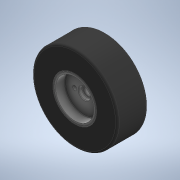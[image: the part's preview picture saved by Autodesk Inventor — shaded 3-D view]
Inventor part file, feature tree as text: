
AUTODESK INVENTOR PART (.ipt)
format: ipt  version: 2022 (Build 260153000, 153)  size: 370,688 bytes
history: native  units: in
note: dims shown in document units (in); Inventor stores cm internally (conversion verified against a paired STEP export)
features: fillet x3, sketch x3, extrude x2, revolve x1
ambient origin geometry x8: Origin, YZ Plane, XZ Plane, XY Plane, X Axis, Y Axis, Z Axis, Center Point
bodies: Solid1 (feature_tree)
feature tree (9):
  revolve  "Revolution1"  [1 undecoded]
  fillet  "Fillet1"  Radius=0.6875in
  fillet  "Fillet2"  Radius=0.0625in
  extrude  "Extrusion1"  Depth=0.125in
  extrude  "Extrusion2"  Depth=0.1875in
  fillet  "Fillet3"  Radius=0.3125in
  sketch  "Sketch1"  dims[d0=1.4in d1=1.0in d2=0.6875in d3=0.0625in]
  sketch  "Sketch2"  dims[d4=0.3125in d5=0.5625in d6=0.125in]
  sketch  "Sketch3"  dims[d7=0.275in d9=0.1875in d10=0.3125in d11=0.125in d12=360.0deg d13=0.0197in d14=0.0039in d15=0.0197in d16=0.0039in d17=0.0312in d18=0.0625in d19=0.625in d20=0.325in d21=0.64in d22=0.15in d23=0.25in d24=0.7874in d26=360.0deg d28=1.0in d29=0.0in d30=0.625in d31=0.138in d32=0.7874in d34=360.0deg d36=0.0in d37=0.0in d38=0.0197in]
note: 1 required parameter value undecoded (feature->parameter linkage not recoverable at this tier; creation-order binding heuristic only, values carry confidence <= 0.55)
